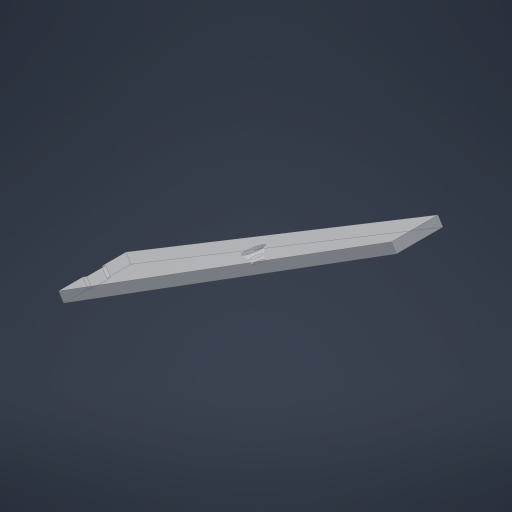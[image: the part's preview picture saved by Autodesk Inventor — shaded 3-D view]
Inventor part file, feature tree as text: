
AUTODESK INVENTOR PART (.ipt)
format: ipt  version: 2023 (Build 270158000, 158)  size: 222,208 bytes
history: native  units: in
note: dims shown in document units (in); Inventor stores cm internally (conversion verified against a paired STEP export)
features: sketch x5, plane x2, extrude x2, hole x1
ambient origin geometry x8: Origin, YZ Plane, XZ Plane, XY Plane, X Axis, Y Axis, Z Axis, Center Point
bodies: Solid1 (feature_tree)
feature tree (10):
  sketch  "Sketch1"  dims[d0=34.0in d1=8.511in]
  plane  "Work Plane1"
  sketch  "Sketch2"  dims[d2=23.5in d3=90.0deg]
  plane  "Work Plane2"
  extrude  "Extrusion1"  Depth=8.511in
  extrude  "Extrusion3"  TaperAngle=90.0deg  [1 undecoded]
  hole  "Hole1"  [1 undecoded]
  sketch  "Sketch3"  dims[d4=0.0412in d5=90.0deg]
  sketch  "Sketch5"  dims[d6=0.0412in]
  sketch  "Sketch6"  dims[d7=0.25in d8=0.0in d17=0.25in d18=0.5in d19=0.0in d20=0.0in d21=9.9962in d22=4.9981in d23=0.266in d24=0.75in d25=0.507in d26=0.25in d27=0.5635in d28=0.536in d29=0.0in d9=0.5in d10=0.0344in]
note: 2 required parameter values undecoded (feature->parameter linkage not recoverable at this tier; creation-order binding heuristic only, values carry confidence <= 0.55)
